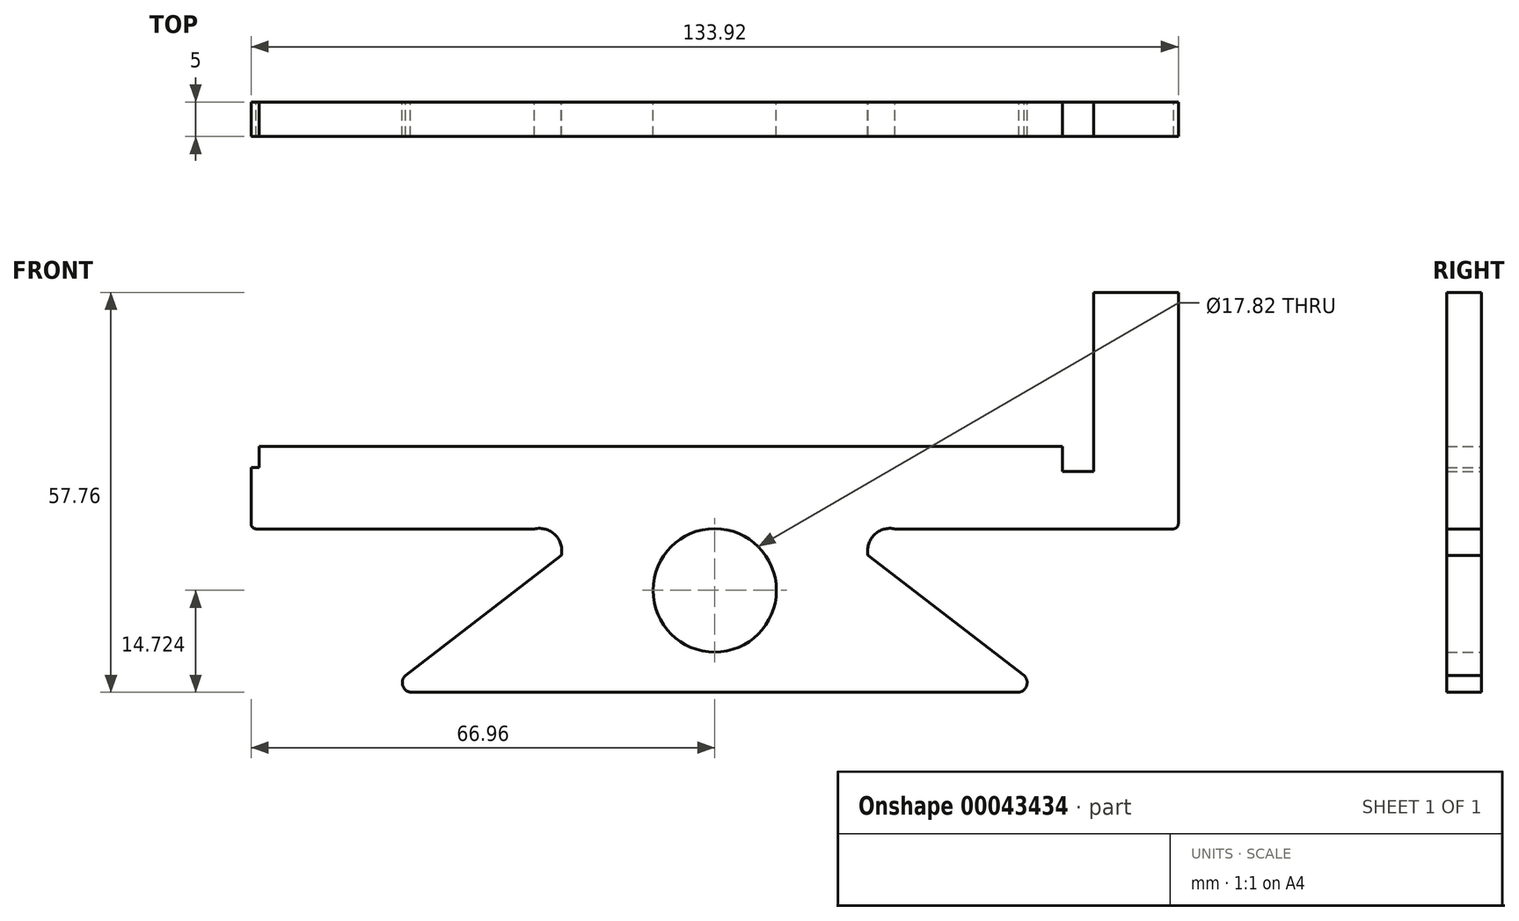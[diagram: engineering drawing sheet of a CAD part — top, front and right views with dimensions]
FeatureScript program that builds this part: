
annotation { "Feature Type Name" : "Feature", "Feature Type Description" : "" }
export const myFeature = defineFeature(function(context is Context, id is Id, definition is map)
    precondition{}
    {
        {
            var Q0;
            Q0=qCreatedBy(makeId("Front.planeOp"),FACE);
            var sketch = newSketch(context, id + "F0", { "sketchPlane" : qUnion([Q0])});
            skLineSegment(sketch, "E0", {"start": v(0, 11.94) * mm, "end": v(-66.05, 11.94) * mm});
            skLineSegment(sketch, "E1", {"start": v(-66.96, 8.84) * mm, "end": v(-66.96, 0.8) * mm});
            skLineSegment(sketch, "E2", {"start": v(-66.26, 0) * mm, "end": v(-26.04, 0) * mm});
            skLineSegment(sketch, "E3", {"start": v(-22.15, -3.84) * mm, "end": v(-44.67, -21.15) * mm});
            skLineSegment(sketch, "E4", {"start": v(-43.94, -23.6) * mm, "end": v(0, -23.6) * mm});
            skArc(sketch, "E5", {"start": v(-22.15, -3.84) * mm, "mid": v(-23.04, -0.85) * mm, "end": v(-26.04, 0) * mm});
            skPoint(sketch, "E6.orphan", {"position": v(0, 0) * mm});
            skLineSegment(sketch, "E7", {"start": v(0, 0.03) * mm, "end": v(0, 0) * mm, "construction": true});
            skArc(sketch, "E8", {"start": v(-66.96, 0.8) * mm, "mid": v(-66.69, 0.2) * mm, "end": v(-66.05, 0) * mm});
            skArc(sketch, "E9", {"start": v(-65.8, 11.94) * mm, "mid": v(-65.92, 11.95) * mm, "end": v(-66.05, 11.94) * mm});
            skArc(sketch, "E10", {"start": v(-44.46, -21) * mm, "mid": v(-45.1, -22.48) * mm, "end": v(-43.94, -23.6) * mm});
            skPoint(sketch, "E11.orphan", {"position": v(-66.96, 0) * mm});
            skLineSegment(sketch, "E12.MirrorCS", {"start": v(0, 11.94) * mm, "end": v(50.25, 11.94) * mm});
            skLineSegment(sketch, "E13.MirrorCS", {"start": v(66.96, 10.8) * mm, "end": v(66.96, 0.8) * mm});
            skArc(sketch, "E14.MirrorCS", {"start": v(66.96, 0.8) * mm, "mid": v(66.69, 0.2) * mm, "end": v(66.05, 0) * mm});
            skLineSegment(sketch, "E15.MirrorCS", {"start": v(66.26, 0) * mm, "end": v(26.04, 0) * mm});
            skArc(sketch, "E16.MirrorCS", {"start": v(22.15, -3.84) * mm, "mid": v(23.04, -0.85) * mm, "end": v(26.04, 0) * mm});
            skLineSegment(sketch, "E17.MirrorCS", {"start": v(22.15, -3.84) * mm, "end": v(44.67, -21.15) * mm});
            skArc(sketch, "E18.MirrorCS", {"start": v(44.46, -21) * mm, "mid": v(45.1, -22.48) * mm, "end": v(43.94, -23.6) * mm});
            skLineSegment(sketch, "E19.MirrorCS", {"start": v(43.94, -23.6) * mm, "end": v(0, -23.6) * mm});
            skLineSegment(sketch, "E20", {"start": v(66.96, 0.8) * mm, "end": v(66.96, 34.16) * mm});
            skLineSegment(sketch, "E21", {"start": v(66.96, 34.16) * mm, "end": v(54.72, 34.16) * mm});
            skLineSegment(sketch, "E22", {"start": v(54.72, 34.16) * mm, "end": v(54.72, 8.27) * mm});
            skLineSegment(sketch, "E23", {"start": v(50.25, 11.94) * mm, "end": v(50.25, 8.27) * mm});
            skLineSegment(sketch, "E24", {"start": v(50.25, 8.27) * mm, "end": v(54.72, 8.27) * mm});
            skLineSegment(sketch, "E25", {"start": v(-65.8, 11.94) * mm, "end": v(-65.8, 8.84) * mm});
            skLineSegment(sketch, "E26", {"start": v(-65.8, 8.84) * mm, "end": v(-66.96, 8.84) * mm});
            skPoint(sketch, "E27.orphan", {"position": v(-66.96, 10.8) * mm});
            skArc(sketch, "E28.trimOffspring", {"start": v(66.96, 11) * mm, "mid": v(66.97, 10.9) * mm, "end": v(66.96, 10.8) * mm});
            skPoint(sketch, "E29.MirrorCS.end.orphan", {"position": v(66.05, 11.94) * mm});
            skPoint(sketch, "E29.MirrorCS.start.orphan", {"position": v(65.8, 11.94) * mm});
            skCircle(sketch, "E30", {"center": v(0, -8.88) * mm, "radius": 8.9 * mm});
            skPoint(sketch, "E31.orphan", {"position": v(0, 41.07) * mm});
            skLineSegment(sketch, "E32.trimOffspring", {"start": v(0, 0) * mm, "end": v(0, 0.03) * mm});
            skSolve(sketch);
        }
        {
            var Q0;
            {var subQ19=sQuery(id+"F0.wireOp",EDGE,"E1");Q0=makeQuery(id+"F0.imprint","IMPRINT",FACE,{"disambiguationData":[TD([[makeQuery(id+"F0.imprint","IMPRINT",EDGE,{"derivedFrom":subQ19}),1.0]])]});}
            extrude(context, id + "F1", {"entities" : qUnion([Q0]), "depth" : 5 * mm});
        }
    });
